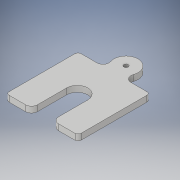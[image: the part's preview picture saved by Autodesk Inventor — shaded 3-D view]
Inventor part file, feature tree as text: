
AUTODESK INVENTOR PART (.ipt)
format: ipt  version: 2018 (Build 220112000, 112)  size: 136,192 bytes
history: native  units: in
note: dims shown in document units (in); Inventor stores cm internally (conversion verified against a paired STEP export)
features: extrude x1, sketch x1, fillet x1
ambient origin geometry x8: Origin, YZ Plane, XZ Plane, XY Plane, X Axis, Y Axis, Z Axis, Center Point
bodies: Solid1 (feature_tree)
feature tree (3):
  extrude  "Extrusion1"  Depth=1.0in TaperAngle=0.0deg
  sketch  "Sketch1"  dims[d0=0.091in d1=1.0in d2=0.0in]
  fillet  "Fillet2"  [1 undecoded]
note: 1 required parameter value undecoded (feature->parameter linkage not recoverable at this tier; creation-order binding heuristic only, values carry confidence <= 0.55)
